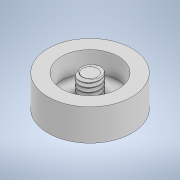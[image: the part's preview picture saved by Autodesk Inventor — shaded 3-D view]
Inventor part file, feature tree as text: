
AUTODESK INVENTOR PART (.ipt)
format: ipt  version: 2020 (Build 240168000, 168)  size: 544,768 bytes
history: native  units: in
note: dims shown in document units (in); Inventor stores cm internally (conversion verified against a paired STEP export)
features: sketch x6, extrude x3, revolve x2, thread x1, helix x1
ambient origin geometry x8: Origin, YZ Plane, XZ Plane, XY Plane, X Axis, Y Axis, Z Axis, Center Point
bodies: Solid1 (feature_tree), Solid3 (feature_tree)
feature tree (13):
  extrude  "Extrusion1"  Depth=0.375in TaperAngle=0.0deg
  extrude  "Extrusion2"  Depth=0.25in TaperAngle=0.0deg
  extrude  "Extrusion3"  Depth=0.25in TaperAngle=0.0deg
  thread  "Thread1"  [1 undecoded]
  revolve  "Revolution3"  [1 undecoded]
  revolve  "Revolution4"  [1 undecoded]
  helix  "Coil2"  [1 undecoded]
  sketch  "Sketch1"  dims[d0=1.0in d1=0.375in d2=0.0in]
  sketch  "Sketch2"  dims[d3=0.675in d4=0.25in d5=0.0in]
  sketch  "Sketch3"  dims[d6=0.25in d7=0.25in d8=0.0in d9=0.25in d10=0.0in]
  sketch  "Sketch7"  dims[d18=0.3779in d30=0.3779in d31=0.008in d32=0.008in]
  sketch  "Sketch8"  dims[d35=0.05in d37=0.3779in d39=0.0in]
  sketch  "Sketch9"  dims[d40=0.0in d41=0.05in d42=0.35in d43=0.3937in d44=0.0in d45=0.0in d46=0.0in d47=0.0in d48=0.0in]
note: 4 required parameter values undecoded (feature->parameter linkage not recoverable at this tier; creation-order binding heuristic only, values carry confidence <= 0.55)